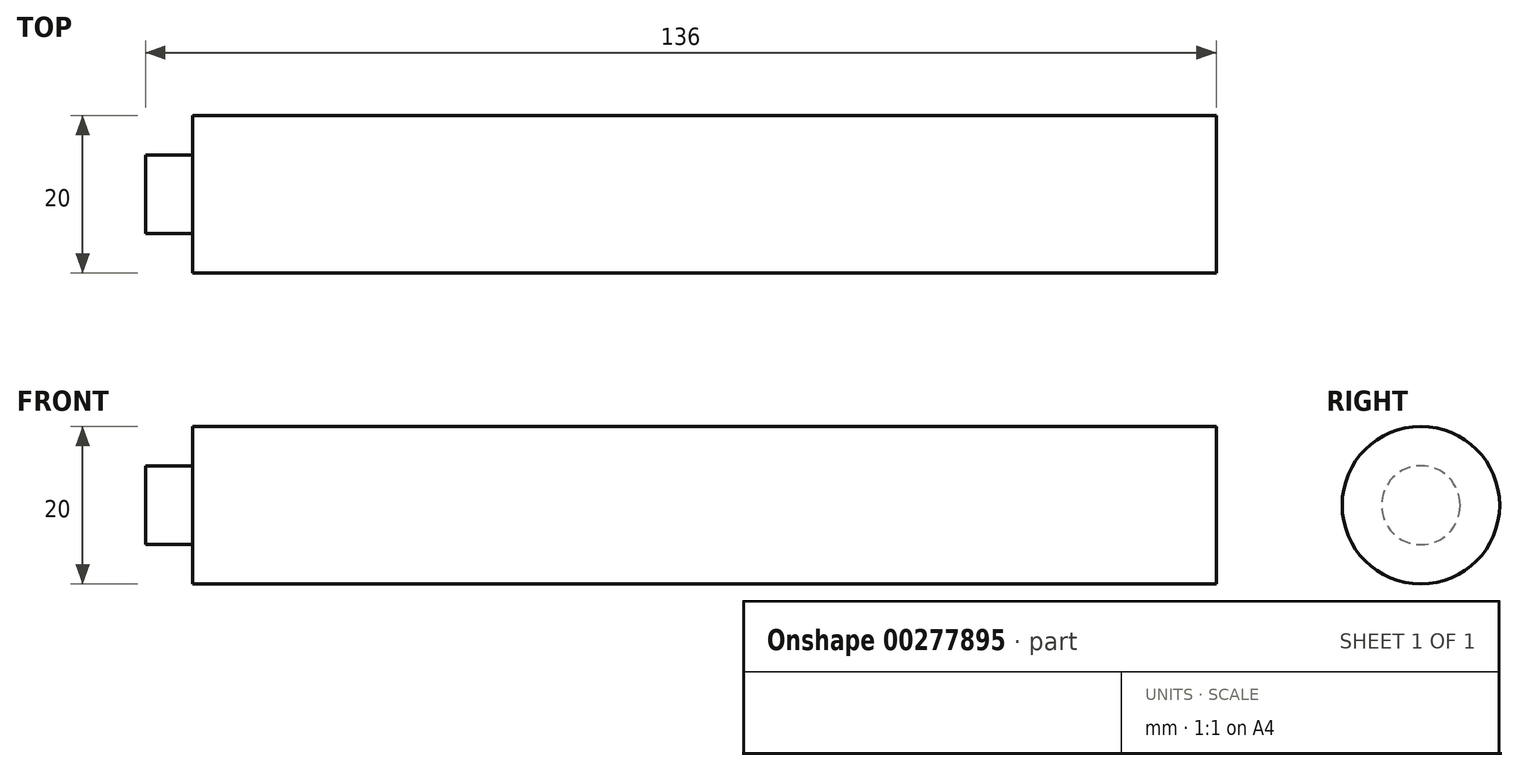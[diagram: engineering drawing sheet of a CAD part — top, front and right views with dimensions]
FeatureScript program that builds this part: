
annotation { "Feature Type Name" : "Feature", "Feature Type Description" : "" }
export const myFeature = defineFeature(function(context is Context, id is Id, definition is map)
    precondition{}
    {
        {
            var Q0;
            Q0=qCreatedBy(makeId("Front.planeOp"),FACE);
            var sketch = newSketch(context, id + "F0", { "sketchPlane" : qUnion([Q0])});
            skLineSegment(sketch, "E0", {"start": v(0, 0) * mm, "end": v(136, 0) * mm});
            skLineSegment(sketch, "E1", {"start": v(136, 0) * mm, "end": v(136, 10) * mm});
            skLineSegment(sketch, "E2", {"start": v(136, 10) * mm, "end": v(6, 10) * mm});
            skLineSegment(sketch, "E3", {"start": v(6, 10) * mm, "end": v(6, 5) * mm});
            skLineSegment(sketch, "E4", {"start": v(6, 5) * mm, "end": v(0, 5) * mm});
            skLineSegment(sketch, "E5", {"start": v(0, 5) * mm, "end": v(0, 0) * mm});
            skSolve(sketch);
        }
        {
            var Q0;
            Q0=makeQuery(id+"F0.imprint","IMPRINT",FACE,{"disambiguationData":[TD([[makeQuery(id+"F0.imprint","IMPRINT",EDGE,{"derivedFrom":sQuery(id+"F0.wireOp",EDGE,"E0")}),1.0]])]});
            var Q1;
            Q1=sQuery(id+"F0.wireOp",EDGE,"E0");
            revolve(context, id + "F1", {"entities" : qUnion([Q0]), "axis" : qUnion([Q1]), "revolveType" : RevolveType.FULL});
        }
    });
